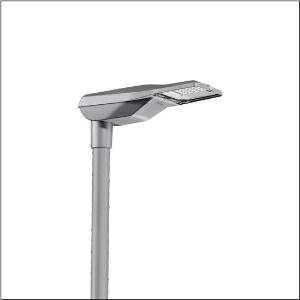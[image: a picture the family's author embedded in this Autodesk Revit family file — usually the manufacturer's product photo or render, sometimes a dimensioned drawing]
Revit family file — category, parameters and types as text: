
# Revit family: streetlight_sl_21_iq_micro___stw1_0a_5xe1e31d08cb_0f3c
name_source: partatom
category: Lighting Fixtures
units: mm (PartAtom-declared; Revit-internal decimal feet)

## family parameters
Cut with Voids When Loaded = No
Host = Face
Light Source = No
Part Type = Normal
Room Calculation Point = No
Round Connector Dimension = Use Diameter
Shared = No

## types (1)
- --- (1 x LED, 2870 lm, 19.4 W, 3000K)
    Apparent Load = 19 VA
    CIE Flux Codes = 38 75 98 100 100
    Color Rendering = 70
    Color Temperature = 3000K
    Default Elevation = 1800 mm
    Description = Streetlight SL 21 iQ micro, mast luminaire, primary light control with lens, of PMMA, primary optical cover: cover, of toughened safety glass, transparent, light distribution: STW1.0a, light emission: direct distribution, primary light characteristic: asymmetric, installation type: post-top, side-entry, LED, High Power LED, rated luminous flux: 2.870lm, luminous efficacy: 148lm/W, light colour: 730, colour temperature: 3000K, control: Auto-Match, Temp-Guard, Lumen-Switch, Night-Set, Smart-Wire, Light-Fading, Desk-Remote (wireless, voltage-free reading and setting of iQ features in the workshop via application-optimized NFC function/RFID function), optimised constant luminous flux control (CLO 2.0), presetting dimming linear, mains connection: 220..240V, AC, 50/60Hz, start of lifetime: 19W, end of service life: 20W, reduction: 10W, luminaire housing, of diecast aluminium, powder-coated, Siteco® metallic grey (DB 702S), corrosivity category C5 mid according to DIN EN ISO 12944, please order mast flange separately, inclination adjustable: 0°, 5°, 10°, 15°, sealing non-destructively replaceable, multi-level sealing system, length: 528mm, width: 235mm, height: 110mm, mast flange for spigot size: 42mm (side-entry): 5XC10008XM4, 60/48mm (side-entry/post-top): 5XC10108XM2, 76/60mm (side-entry/post-top): 5XC10108XM1, protection rating (complete): IP66, insulation class (complete): insulation class II (safety insulation), certification: CE, ENEC, ENEC+, VDE, impact resistance: IK09, permissible operating ambient temperature for outdoor applications: -40..+50°C, standard-compliant lighting for roads and squares, packaging unit: 1 piece

Light Distribution: STW1.0a
    Height = 110 mm
    Lamp = 1 x LED
    Lamp Light Flux = 2870 lm
    Lamp Power = 19.4 W
    Lamp count = 1
    Length = 528 mm
    Luminous efficacy = 148 lm/W
    Manufacturer = Siteco
    ModVariant = No
    Model = 5XE1E31D08CB
    Number of Poles = 1
    OnlyDefault = Yes
    Power Factor = 1
    Product Name = Streetlight SL 21 iQ micro | STW1.0a
    Product group = mast luminaire | pylon top
    ProductGroupID = 6100
    Protection Class = Protection class II
    Protection Degree = IP 66
    RLX_Detail_Level = 1
    RLX_Emergency_Light_Flux = 0 lm
    RLX_Emergency_Type = 0
    RLX_Emergency_Type_DB = No
    RlxData = <blob elided: 98505 chars, md5=dd5803d1>
    Socket = socket
    Standby Power = 0 W
    System Light Flux = 2870 lm
    System Power = 19 W
    Type Comments = factory setting: luminous flux: 100 % | dim-lin: 254 | 387 mA
    Type Image = l_1006881.jpg
    URL = http://relux.com
    VarID = @adj_088265
    Voltage = 0 V
    Weight = 0.00 kg
    Width = 235 mm

## geometry (parser evidence)
native form markers: Blend x4, Sweep x12
no freeform markers — native parametric forms only
